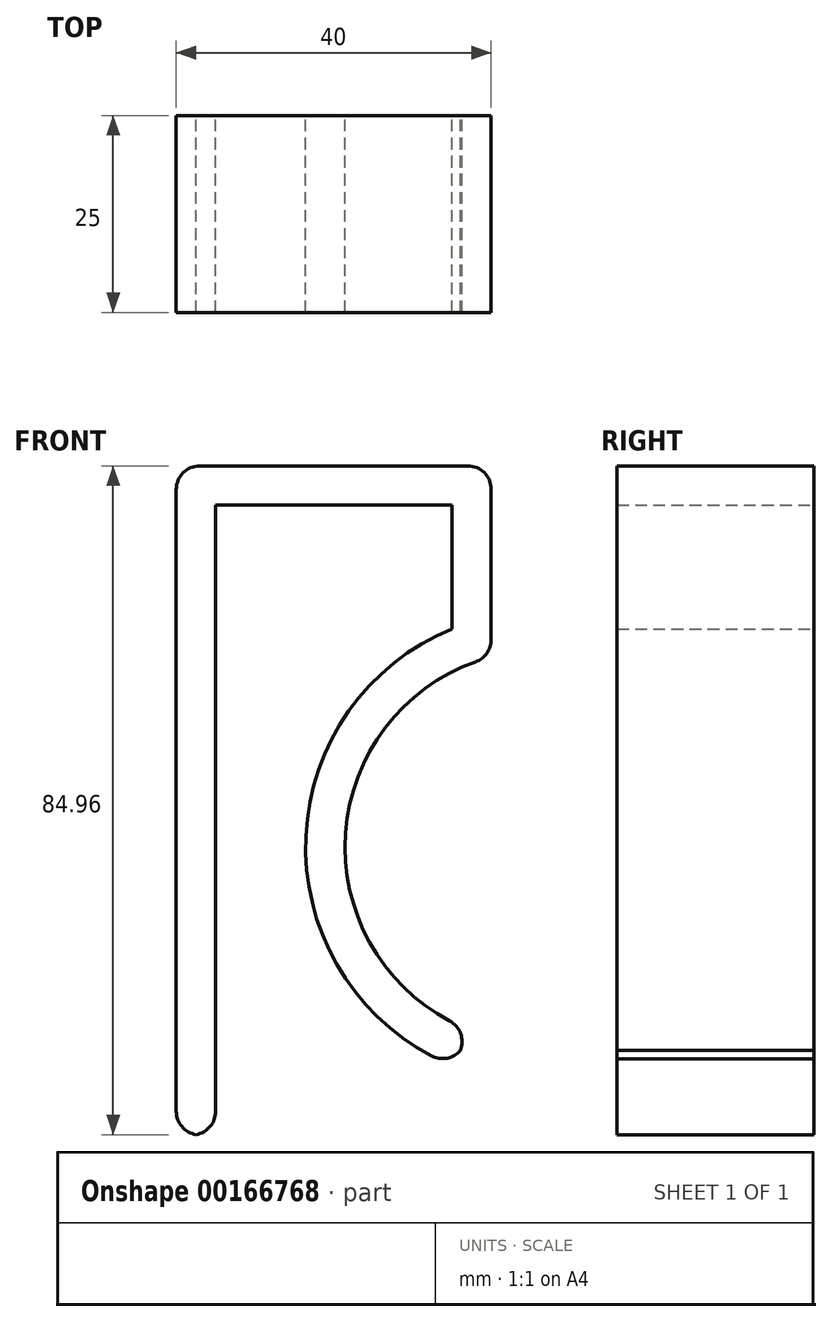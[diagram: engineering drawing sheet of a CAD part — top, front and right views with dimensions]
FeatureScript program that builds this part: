
annotation { "Feature Type Name" : "Feature", "Feature Type Description" : "" }
export const myFeature = defineFeature(function(context is Context, id is Id, definition is map)
    precondition{}
    {
        {
            var Q0;
            Q0=qCreatedBy(makeId("Front.planeOp"),FACE);
            var sketch = newSketch(context, id + "F0", { "sketchPlane" : qUnion([Q0])});
            skLineSegment(sketch, "E0", {"start": v(0, -80) * mm, "end": v(0, 0) * mm});
            skLineSegment(sketch, "E1", {"start": v(30, 0) * mm, "end": v(30, -15.7) * mm});
            skArc(sketch, "E2", {"start": v(30, -15.7) * mm, "mid": v(11.43, -43.43) * mm, "end": v(30, -71.17) * mm});
            skLineSegment(sketch, "E3", {"start": v(0, 0) * mm, "end": v(30, 0) * mm});
            skArc(sketch, "E4.0", {"start": v(35, -19.27) * mm, "mid": v(16.46, -42.17) * mm, "end": v(32.61, -66.82) * mm});
            skLineSegment(sketch, "E4.1", {"start": v(35, 5) * mm, "end": v(35, -19.27) * mm});
            skLineSegment(sketch, "E4.2", {"start": v(-5, 5) * mm, "end": v(35, 5) * mm});
            skLineSegment(sketch, "E4.3", {"start": v(-5, -80) * mm, "end": v(-5, 5) * mm});
            skLineSegment(sketch, "E5", {"start": v(-5, -80) * mm, "end": v(0, -80) * mm});
            skLineSegment(sketch, "E6", {"start": v(30, -71.17) * mm, "end": v(32.61, -66.82) * mm});
            skSolve(sketch);
        }
        {
            var Q0;
            Q0 = qSketchRegion(id + "F0", true);
            extrude(context, id + "F1", {"entities" : qUnion([Q0]), "depth" : 25 * mm});
        }
        {
            var Q0;
            Q0=makeQuery(id+"F1.opExtrude","SWEPT_EDGE",EDGE,{"disambiguationData":[OSD([sQuery(id+"F0.wireOp",EDGE,"E4.1"),sQuery(id+"F0.wireOp",EDGE,"E4.2")])]});
            var Q1;
            Q1=makeQuery(id+"F1.opExtrude","SWEPT_EDGE",EDGE,{"disambiguationData":[OSD([sQuery(id+"F0.wireOp",EDGE,"E4.0"),sQuery(id+"F0.wireOp",EDGE,"E4.1")])]});
            var Q2;
            Q2=makeQuery(id+"F1.opExtrude","SWEPT_EDGE",EDGE,{"disambiguationData":[OSD([sQuery(id+"F0.wireOp",EDGE,"E4.0"),sQuery(id+"F0.wireOp",EDGE,"E6")])]});
            var Q3;
            Q3=makeQuery(id+"F1.opExtrude","SWEPT_EDGE",EDGE,{"disambiguationData":[OSD([sQuery(id+"F0.wireOp",EDGE,"E2"),sQuery(id+"F0.wireOp",EDGE,"E6")])]});
            var Q4;
            Q4=makeQuery(id+"F1.opExtrude","SWEPT_EDGE",EDGE,{"disambiguationData":[OSD([sQuery(id+"F0.wireOp",EDGE,"E0"),sQuery(id+"F0.wireOp",EDGE,"E5")])]});
            var Q5;
            Q5=makeQuery(id+"F1.opExtrude","SWEPT_EDGE",EDGE,{"disambiguationData":[OSD([sQuery(id+"F0.wireOp",EDGE,"E4.3"),sQuery(id+"F0.wireOp",EDGE,"E5")])]});
            var Q6;
            Q6=makeQuery(id+"F1.opExtrude","SWEPT_EDGE",EDGE,{"disambiguationData":[OSD([sQuery(id+"F0.wireOp",EDGE,"E4.2"),sQuery(id+"F0.wireOp",EDGE,"E4.3")])]});
            fillet(context, id + "F2", {"entities" : qUnion([Q0, Q1, Q2, Q3, Q4, Q5, Q6]), "radius" : 3 * mm, "tangentPropagation" : true, "allowEdgeOverflow" : false});
        }
    });
